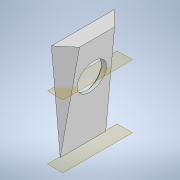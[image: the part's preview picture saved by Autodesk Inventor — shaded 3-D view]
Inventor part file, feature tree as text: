
AUTODESK INVENTOR PART (.ipt)
format: ipt  version: 2021 (Build 250183000, 183)  size: 377,856 bytes
history: native  units: in
note: dims shown in document units (in); Inventor stores cm internally (conversion verified against a paired STEP export)
features: extrude x7, sketch x7, plane x2
ambient origin geometry x8: Origin, YZ Plane, XZ Plane, XY Plane, X Axis, Y Axis, Z Axis, Center Point
bodies: Solid1 (feature_tree)
feature tree (16):
  extrude  "MainStructure"  Depth=0.5622in
  extrude  "PipeHole"  TaperAngle=0.0deg  [1 undecoded]
  extrude  "AngleForTopRelief"  TaperAngle=0.0deg  [1 undecoded]
  extrude  "TextForBack"  TaperAngle=0.0deg  [1 undecoded]
  extrude  "ReliefForHole"  Depth=0.1in TaperAngle=0.0deg
  extrude  "TextForSmallText"  TaperAngle=45.0deg  [1 undecoded]
  plane  "Work Plane1"
  extrude  "SideAngle"  Depth=2.5in
  plane  "Work Plane2"
  sketch  "Sketch1"  dims[d1=0.055in d2=0.5622in]
  sketch  "Sketch2"  dims[d4=0.0in d7=0.0in d8=0.0in]
  sketch  "Sketch6"  dims[d19=0.0in d20=0.0in d25=0.0in]
  sketch  "Sketch7"  dims[d28=0.0in d29=0.0in]
  sketch  "Sketch8"  dims[d35=0.375in d36=0.1in d37=0.0in]
  sketch  "Sketch9"  dims[d38=45.0deg d39=45.0deg]
  sketch  "Sketch10"  dims[d40=0.0in d41=0.0in d42=2.5in]
note: 4 required parameter values undecoded (feature->parameter linkage not recoverable at this tier; creation-order binding heuristic only, values carry confidence <= 0.55)
